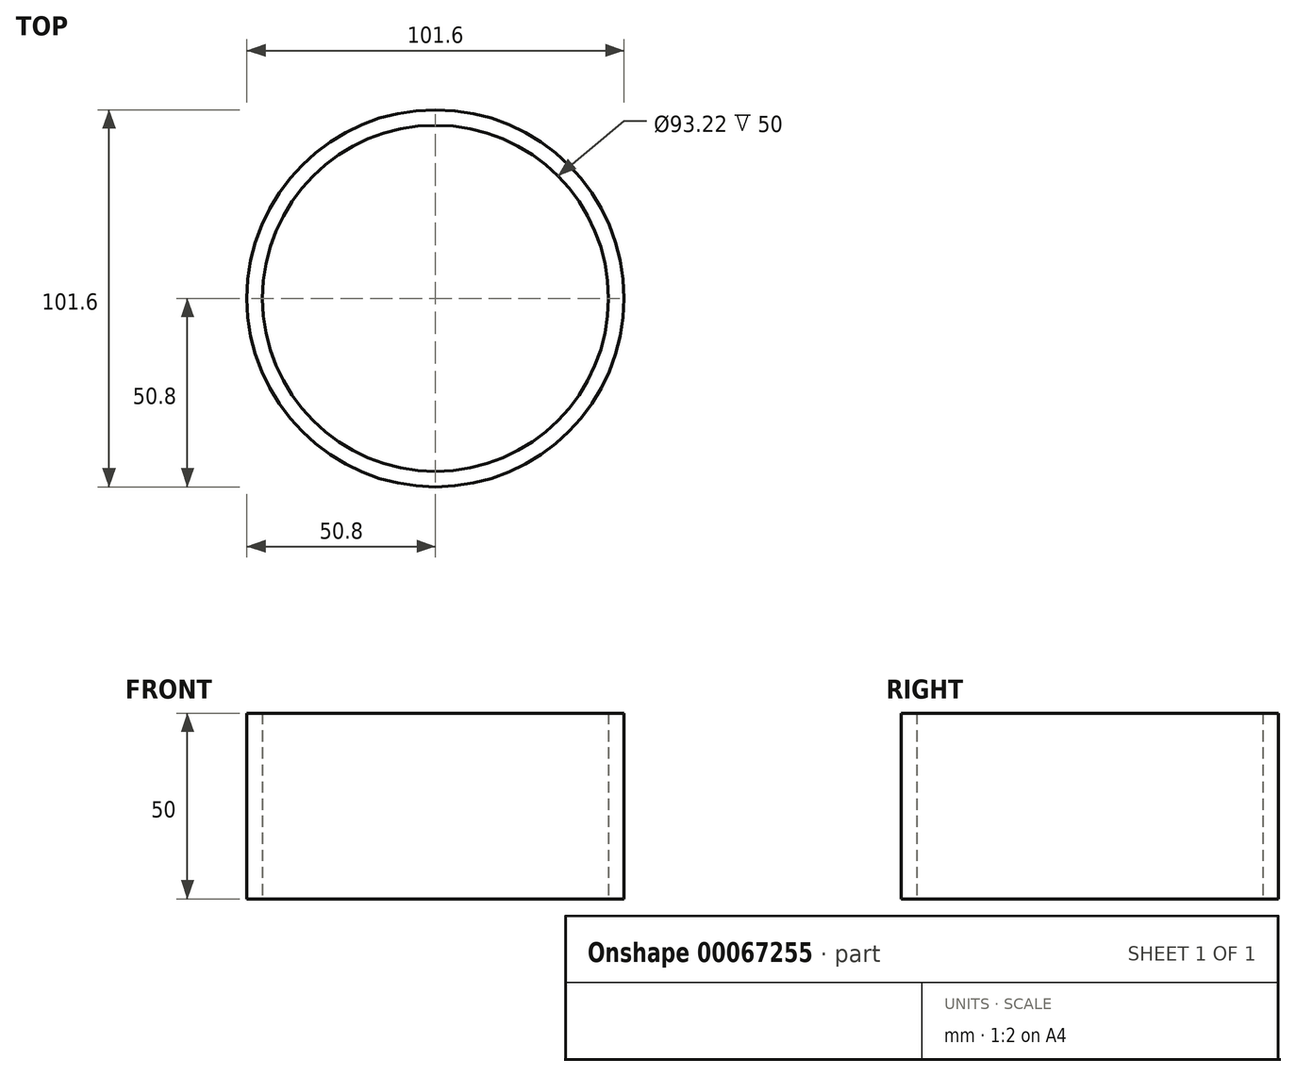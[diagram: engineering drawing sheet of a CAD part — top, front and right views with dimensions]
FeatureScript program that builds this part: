
annotation { "Feature Type Name" : "Feature", "Feature Type Description" : "" }
export const myFeature = defineFeature(function(context is Context, id is Id, definition is map)
    precondition{}
    {
        {
            var Q0;
            Q0=qCreatedBy(makeId("Top.planeOp"),FACE);
            var sketch = newSketch(context, id + "F0", { "sketchPlane" : qUnion([Q0])});
            skCircle(sketch, "E0", {"center": v(0, 0) * mm, "radius": 50.8 * mm});
            skCircle(sketch, "E1", {"center": v(0, 0) * mm, "radius": 46.6 * mm});
            skSolve(sketch);
        }
        {
            var Q0;
            Q0=makeQuery(id+"F0.imprint","IMPRINT",FACE,{"disambiguationData":[TD([[makeQuery(id+"F0.imprint","IMPRINT",EDGE,{"derivedFrom":sQuery(id+"F0.wireOp",EDGE,"E0")}),-1.0]])]});
            var Q1;
            Q1=makeQuery(id+"F0.imprint","IMPRINT",FACE,{"disambiguationData":[TD([[makeQuery(id+"F0.imprint","IMPRINT",EDGE,{"derivedFrom":sQuery(id+"F0.wireOp",EDGE,"E0")}),1.0]])]});
            extrude(context, id + "F1", {"entities" : qUnion([Q0, Q1]), "depth" : 50 * mm});
        }
    });
